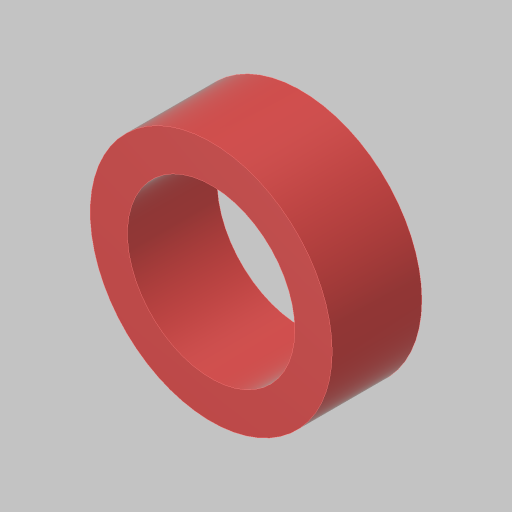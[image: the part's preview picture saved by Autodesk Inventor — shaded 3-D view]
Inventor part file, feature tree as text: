
AUTODESK INVENTOR PART (.ipt)
format: ipt  version: 2023.5 (Build 275446000, 446)  size: 110,592 bytes
history: native  units: in
note: dims shown in document units (in); Inventor stores cm internally (conversion verified against a paired STEP export)
features: extrude x1, sketch x1
ambient origin geometry x8: Origin, YZ Plane, XZ Plane, XY Plane, X Axis, Y Axis, Z Axis, Center Point
bodies: Solid1 (feature_tree)
feature tree (2):
  extrude  "Extrusion1"  Depth=0.3in
  sketch  "Sketch1"  dims[d0=0.56in d1=0.125in d2=0.3in d3=0.0in]
